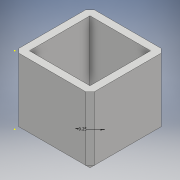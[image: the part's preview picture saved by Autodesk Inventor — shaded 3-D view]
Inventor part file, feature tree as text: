
AUTODESK INVENTOR PART (.ipt)
format: ipt  version: 2017 (Build 210142000, 142)  size: 111,104 bytes
history: native  units: mm
features: sketch x4, extrude x2, chamfer x1
ambient origin geometry x8: Origin, YZ Plane, XZ Plane, XY Plane, X Axis, Y Axis, Z Axis, Center Point
bodies: Solid1 (feature_tree)
feature tree (7):
  extrude  "Extrusion1"  Depth=33.25mm
  sketch  "Sketch2"  dims[d2=30.0mm d3=0.0mm d4=26.75mm]
  extrude  "Extrusion2"  Depth=26.75mm
  chamfer  "Chamfer1"  Distance=26.75mm
  sketch  "Sketch4"  dims[d8=1.875mm d9=2.0mm d10=45.0deg d11=9.25mm]
  sketch  "Sketch1"  dims[d0=33.25mm d1=33.25mm]
  sketch  "Sketch3"  dims[d5=26.75mm d6=26.75mm d7=0.0mm]
